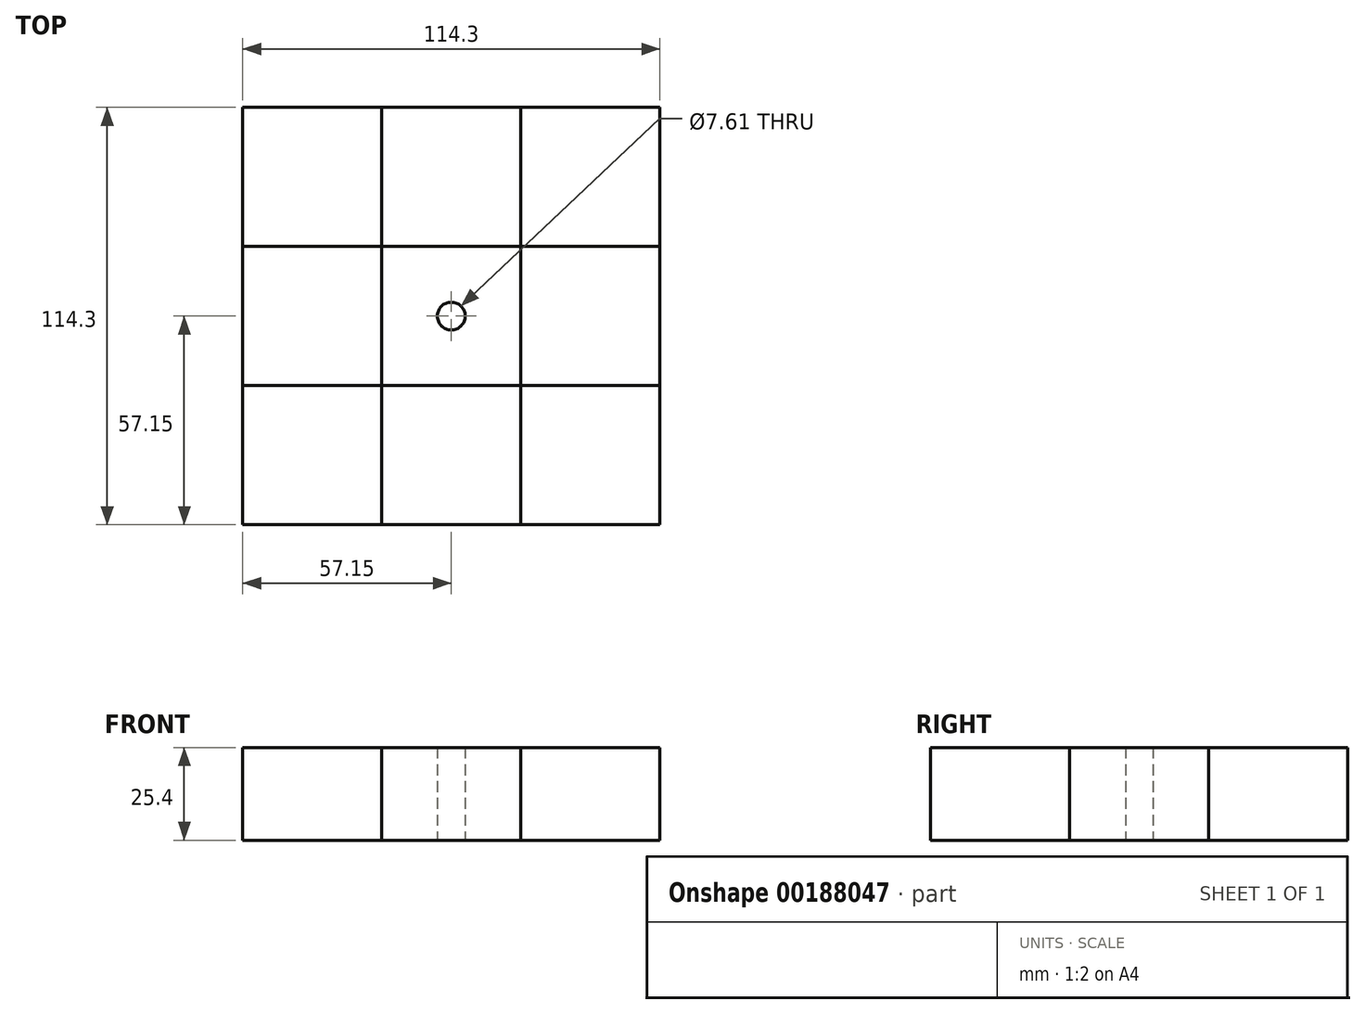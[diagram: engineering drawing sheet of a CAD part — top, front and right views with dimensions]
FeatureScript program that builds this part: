
annotation { "Feature Type Name" : "Feature", "Feature Type Description" : "" }
export const myFeature = defineFeature(function(context is Context, id is Id, definition is map)
    precondition{}
    {
        {
            var Q0;
            Q0=qCreatedBy(makeId("Top.planeOp"),FACE);
            var sketch = newSketch(context, id + "F0", { "sketchPlane" : qUnion([Q0])});
            skLineSegment(sketch, "E0.bottom", {"start": v(57.15, 57.15) * mm, "end": v(-57.15, 57.15) * mm});
            skLineSegment(sketch, "E0.top", {"start": v(57.15, -57.15) * mm, "end": v(-57.15, -57.15) * mm});
            skLineSegment(sketch, "E0.left", {"start": v(57.15, 57.15) * mm, "end": v(57.15, -57.15) * mm});
            skLineSegment(sketch, "E0.right", {"start": v(-57.15, 57.15) * mm, "end": v(-57.15, -57.15) * mm});
            skPoint(sketch, "E0.middle", {"position": v(0, 0) * mm});
            skLineSegment(sketch, "E1", {"start": v(-19.05, 57.15) * mm, "end": v(-19.05, -57.15) * mm});
            skPoint(sketch, "E2", {"position": v(-19.05, 57.15) * mm});
            skPoint(sketch, "E3", {"position": v(-19.05, -57.15) * mm});
            skLineSegment(sketch, "E4", {"start": v(19.05, 57.15) * mm, "end": v(19.05, -57.15) * mm});
            skPoint(sketch, "E5", {"position": v(19.05, 57.15) * mm});
            skPoint(sketch, "E6", {"position": v(19.05, -57.15) * mm});
            skLineSegment(sketch, "E7", {"start": v(-57.15, 19.05) * mm, "end": v(57.15, 19.05) * mm});
            skLineSegment(sketch, "E8", {"start": v(-57.15, -19.05) * mm, "end": v(57.15, -19.05) * mm});
            skPoint(sketch, "E9", {"position": v(-57.15, 19.05) * mm});
            skPoint(sketch, "E10", {"position": v(57.15, 19.05) * mm});
            skPoint(sketch, "E11", {"position": v(57.15, -19.05) * mm});
            skPoint(sketch, "E12", {"position": v(-57.15, -19.05) * mm});
            skPoint(sketch, "E13", {"position": v(-19.05, -19.05) * mm});
            skPoint(sketch, "E14", {"position": v(-19.05, 19.05) * mm});
            skPoint(sketch, "E15", {"position": v(19.05, 19.05) * mm});
            skPoint(sketch, "E16", {"position": v(19.05, -19.05) * mm});
            skSolve(sketch);
        }
        {
            var Q0;
            {var subQ0=sQuery(id+"F0.wireOp",EDGE,"E0.left");var subQ1=sQuery(id+"F0.wireOp",EDGE,"E0.bottom");var subQ2=makeQuery(id+"F0.imprint","INTERSECT",VERTEX,{"derivedFrom":[subQ1,subQ0]});Q0=makeQuery(id+"F0.imprint","IMPRINT",FACE,{"disambiguationData":[TD([[makeQuery(id+"F0.imprint","IMPRINT",EDGE,{"disambiguationData":[TD([[subQ2,-1.0]])],"derivedFrom":subQ1}),1.0]])]});}
            var sketch = newSketch(context, id + "F1", { "sketchPlane" : qUnion([Q0])});
            skSolve(sketch);
        }
        {
            var Q0;
            {var subQ0=sQuery(id+"F0.wireOp",EDGE,"E0.right");var subQ1=sQuery(id+"F0.wireOp",EDGE,"E0.bottom");var subQ2=makeQuery(id+"F0.imprint","INTERSECT",VERTEX,{"derivedFrom":[subQ1,subQ0]});Q0=makeQuery(id+"F0.imprint","IMPRINT",FACE,{"disambiguationData":[TD([[makeQuery(id+"F0.imprint","IMPRINT",EDGE,{"disambiguationData":[TD([[subQ2,1.0]])],"derivedFrom":subQ1}),1.0]])]});}
            var sketch = newSketch(context, id + "F2", { "sketchPlane" : qUnion([Q0])});
            skSolve(sketch);
        }
        {
            var Q0;
            {var subQ0=sQuery(id+"F0.wireOp",EDGE,"E7");var subQ1=sQuery(id+"F0.wireOp",EDGE,"E1");var subQ2=makeQuery(id+"F0.imprint","INTERSECT",VERTEX,{"derivedFrom":[subQ1,subQ0]});Q0=makeQuery(id+"F0.imprint","IMPRINT",FACE,{"disambiguationData":[TD([[makeQuery(id+"F0.imprint","IMPRINT",EDGE,{"disambiguationData":[TD([[subQ2,-1.0]])],"derivedFrom":subQ1}),1.0]])]});}
            var sketch = newSketch(context, id + "F3", { "sketchPlane" : qUnion([Q0])});
            skSolve(sketch);
        }
        {
            var Q0;
            {var subQ0=sQuery(id+"F0.wireOp",EDGE,"E0.left");var subQ1=sQuery(id+"F0.wireOp",EDGE,"E0.top");var subQ2=makeQuery(id+"F0.imprint","INTERSECT",VERTEX,{"derivedFrom":[subQ1,subQ0]});Q0=makeQuery(id+"F0.imprint","IMPRINT",FACE,{"disambiguationData":[TD([[makeQuery(id+"F0.imprint","IMPRINT",EDGE,{"disambiguationData":[TD([[subQ2,-1.0]])],"derivedFrom":subQ1}),-1.0]])]});}
            var sketch = newSketch(context, id + "F4", { "sketchPlane" : qUnion([Q0])});
            skSolve(sketch);
        }
        {
            var Q0;
            {var subQ0=sQuery(id+"F0.wireOp",EDGE,"E0.right");var subQ1=sQuery(id+"F0.wireOp",EDGE,"E0.top");var subQ2=makeQuery(id+"F0.imprint","INTERSECT",VERTEX,{"derivedFrom":[subQ1,subQ0]});Q0=makeQuery(id+"F0.imprint","IMPRINT",FACE,{"disambiguationData":[TD([[makeQuery(id+"F0.imprint","IMPRINT",EDGE,{"disambiguationData":[TD([[subQ2,1.0]])],"derivedFrom":subQ1}),-1.0]])]});}
            var sketch = newSketch(context, id + "F5", { "sketchPlane" : qUnion([Q0])});
            skSolve(sketch);
        }
        {
            var Q0;
            {var subQ0=sQuery(id+"F0.wireOp",EDGE,"E1");var subQ1=sQuery(id+"F0.wireOp",EDGE,"E0.bottom");var subQ2=makeQuery(id+"F0.imprint","INTERSECT",VERTEX,{"derivedFrom":[subQ1,subQ0]});Q0=makeQuery(id+"F0.imprint","IMPRINT",FACE,{"disambiguationData":[TD([[makeQuery(id+"F0.imprint","IMPRINT",EDGE,{"disambiguationData":[TD([[subQ2,1.0]])],"derivedFrom":subQ1}),1.0]])]});}
            var Q1;
            {var subQ0=sQuery(id+"F0.wireOp",EDGE,"E7");var subQ1=sQuery(id+"F0.wireOp",EDGE,"E0.left");var subQ2=makeQuery(id+"F0.imprint","INTERSECT",VERTEX,{"derivedFrom":[subQ1,subQ0]});Q1=makeQuery(id+"F0.imprint","IMPRINT",FACE,{"disambiguationData":[TD([[makeQuery(id+"F0.imprint","IMPRINT",EDGE,{"disambiguationData":[TD([[subQ2,-1.0]])],"derivedFrom":subQ1}),-1.0]])]});}
            var Q2;
            {var subQ0=sQuery(id+"F0.wireOp",EDGE,"E1");var subQ1=sQuery(id+"F0.wireOp",EDGE,"E0.top");var subQ2=makeQuery(id+"F0.imprint","INTERSECT",VERTEX,{"derivedFrom":[subQ1,subQ0]});Q2=makeQuery(id+"F0.imprint","IMPRINT",FACE,{"disambiguationData":[TD([[makeQuery(id+"F0.imprint","IMPRINT",EDGE,{"disambiguationData":[TD([[subQ2,1.0]])],"derivedFrom":subQ1}),-1.0]])]});}
            var Q3;
            {var subQ0=sQuery(id+"F0.wireOp",EDGE,"E7");var subQ1=sQuery(id+"F0.wireOp",EDGE,"E0.right");var subQ2=makeQuery(id+"F0.imprint","INTERSECT",VERTEX,{"derivedFrom":[subQ1,subQ0]});Q3=makeQuery(id+"F0.imprint","IMPRINT",FACE,{"disambiguationData":[TD([[makeQuery(id+"F0.imprint","IMPRINT",EDGE,{"disambiguationData":[TD([[subQ2,-1.0]])],"derivedFrom":subQ1}),1.0]])]});}
            extrude(context, id + "F6", {"entities" : qUnion([Q0, Q1, Q2, Q3]), "depth" : 25.4 * mm});
        }
        {
            var Q0;
            {var subQ0=sQuery(id+"F0.wireOp",EDGE,"E0.right");var subQ1=sQuery(id+"F0.wireOp",EDGE,"E0.bottom");var subQ2=makeQuery(id+"F0.imprint","INTERSECT",VERTEX,{"derivedFrom":[subQ1,subQ0]});Q0=makeQuery(id+"F2.imprint","IMPRINT",FACE,{"disambiguationData":[TD([[makeQuery(id+"F2.imprint","IMPRINT",EDGE,{"derivedFrom":makeQuery(id+"F0.imprint","IMPRINT",EDGE,{"disambiguationData":[TD([[subQ2,1.0]])],"derivedFrom":subQ1})}),1.0]])]});}
            var Q1;
            {var subQ0=sQuery(id+"F0.wireOp",EDGE,"E7");var subQ1=sQuery(id+"F0.wireOp",EDGE,"E1");var subQ2=makeQuery(id+"F0.imprint","INTERSECT",VERTEX,{"derivedFrom":[subQ1,subQ0]});Q1=makeQuery(id+"F3.imprint","IMPRINT",FACE,{"disambiguationData":[TD([[makeQuery(id+"F3.imprint","IMPRINT",EDGE,{"derivedFrom":makeQuery(id+"F0.imprint","IMPRINT",EDGE,{"disambiguationData":[TD([[subQ2,-1.0]])],"derivedFrom":subQ1})}),1.0]])]});}
            var Q2;
            {var subQ0=sQuery(id+"F0.wireOp",EDGE,"E0.left");var subQ1=sQuery(id+"F0.wireOp",EDGE,"E0.bottom");var subQ2=makeQuery(id+"F0.imprint","INTERSECT",VERTEX,{"derivedFrom":[subQ1,subQ0]});Q2=makeQuery(id+"F1.imprint","IMPRINT",FACE,{"disambiguationData":[TD([[makeQuery(id+"F1.imprint","IMPRINT",EDGE,{"derivedFrom":makeQuery(id+"F0.imprint","IMPRINT",EDGE,{"disambiguationData":[TD([[subQ2,-1.0]])],"derivedFrom":subQ1})}),1.0]])]});}
            var Q3;
            {var subQ0=sQuery(id+"F0.wireOp",EDGE,"E0.left");var subQ1=sQuery(id+"F0.wireOp",EDGE,"E0.top");var subQ2=makeQuery(id+"F0.imprint","INTERSECT",VERTEX,{"derivedFrom":[subQ1,subQ0]});Q3=makeQuery(id+"F4.imprint","IMPRINT",FACE,{"disambiguationData":[TD([[makeQuery(id+"F4.imprint","IMPRINT",EDGE,{"derivedFrom":makeQuery(id+"F0.imprint","IMPRINT",EDGE,{"disambiguationData":[TD([[subQ2,-1.0]])],"derivedFrom":subQ1})}),-1.0]])]});}
            var Q4;
            {var subQ0=sQuery(id+"F0.wireOp",EDGE,"E0.right");var subQ1=sQuery(id+"F0.wireOp",EDGE,"E0.top");var subQ2=makeQuery(id+"F0.imprint","INTERSECT",VERTEX,{"derivedFrom":[subQ1,subQ0]});Q4=makeQuery(id+"F5.imprint","IMPRINT",FACE,{"disambiguationData":[TD([[makeQuery(id+"F5.imprint","IMPRINT",EDGE,{"derivedFrom":makeQuery(id+"F0.imprint","IMPRINT",EDGE,{"disambiguationData":[TD([[subQ2,1.0]])],"derivedFrom":subQ1})}),-1.0]])]});}
            extrude(context, id + "F7", {"entities" : qUnion([Q0, Q1, Q2, Q3, Q4]), "depth" : 25.4 * mm});
        }
        {
            var Q0;
            Q0=qCreatedBy(makeId("Top.planeOp"),FACE);
            var sketch = newSketch(context, id + "F8", { "sketchPlane" : qUnion([Q0])});
            skCircle(sketch, "E17", {"center": v(0, 0) * mm, "radius": 3.8 * mm});
            skSolve(sketch);
        }
        {
            var Q0;
            Q0=makeQuery(id+"F8.imprint","IMPRINT",FACE,{"disambiguationData":[TD([[makeQuery(id+"F8.imprint","IMPRINT",EDGE,{"derivedFrom":sQuery(id+"F8.wireOp",EDGE,"E17")}),1.0]])]});
            extrude(context, id + "F9", {"entities" : qUnion([Q0]), "operationType" : NewBodyOperationType.REMOVE, "depth" : 59.44 * mm});
        }
    });
